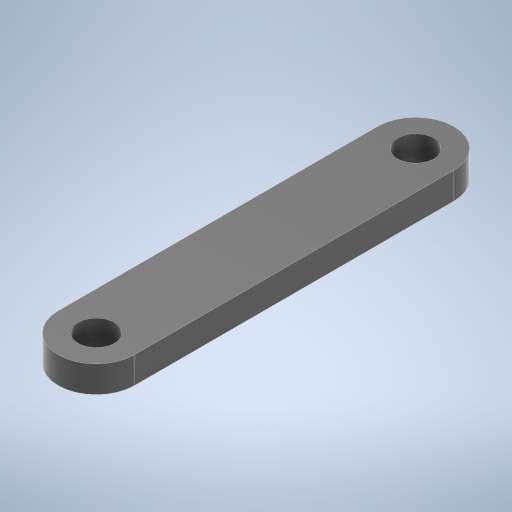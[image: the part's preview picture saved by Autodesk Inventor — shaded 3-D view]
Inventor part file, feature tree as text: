
AUTODESK INVENTOR PART (.ipt)
format: ipt  version: 2024 (Build 280153000, 153)  size: 230,912 bytes
history: native  units: in
note: dims shown in document units (in); Inventor stores cm internally (conversion verified against a paired STEP export)
features: extrude x1, sketch x1
ambient origin geometry x8: Origin, YZ Plane, XZ Plane, XY Plane, X Axis, Y Axis, Z Axis, Center Point
bodies: Solid1 (feature_tree)
feature tree (2):
  extrude  "Extrusion1"  Depth=0.125in
  sketch  "Sketch1"  dims[d0=0.17in d1=0.17in d2=1.5in d3=0.0938in d4=0.0938in d5=0.125in d6=0.0in]
